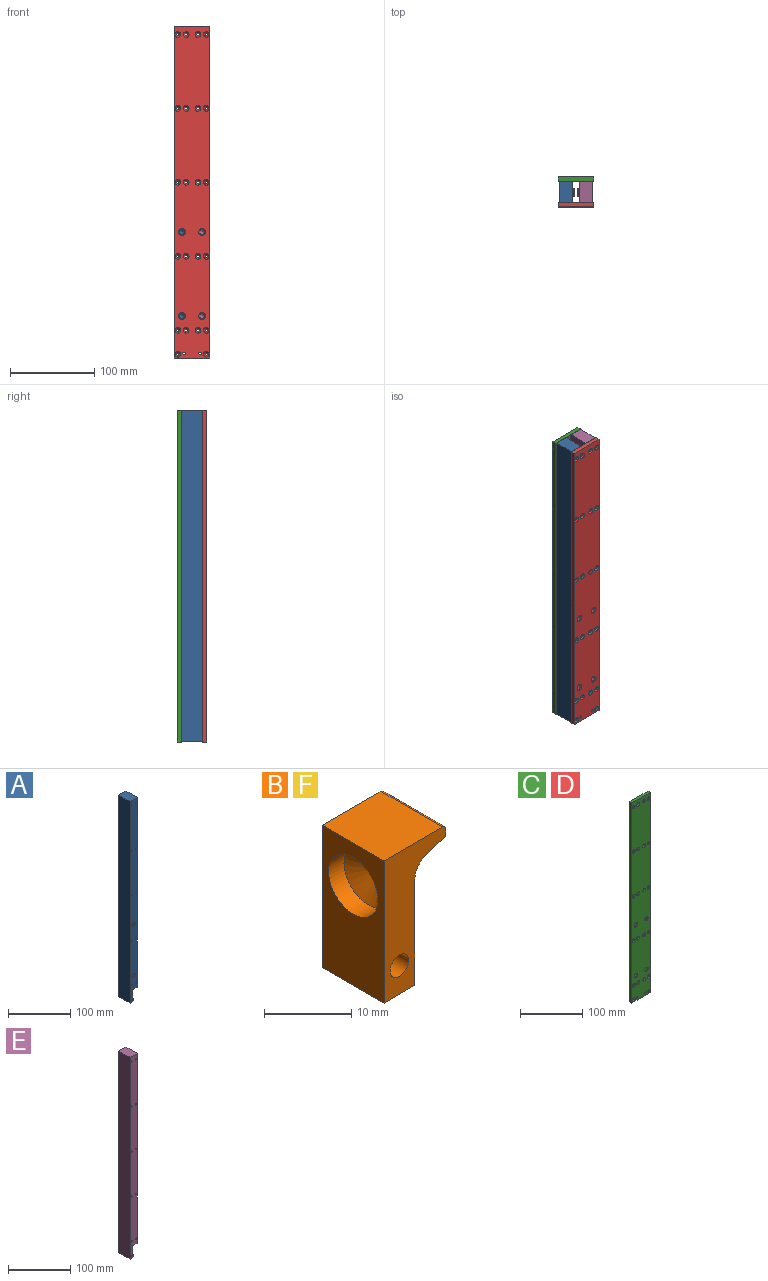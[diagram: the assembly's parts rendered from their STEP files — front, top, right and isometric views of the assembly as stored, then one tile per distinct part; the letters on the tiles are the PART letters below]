
ASSEMBLY  parts=6 mates=5
PART A: 29 faces, bbox 16x25.2x395 mm
  f0: plane 25.2x16mm, normal (0,0,1), area 403.2mm2, adj f1,f3,f4,f5
  f1: plane 395x25.2mm, normal (-1,0,0), area 9954mm2, adj f0,f2,f4,f5
  f2: plane 25.2x8mm, normal (0,0,-1), area 201.6mm2, adj f1,f4,f5,f9
  f3: plane 372x25.2mm, normal (1,0,0), area 9374.4mm2, adj f0,f4,f5,f6
  f4: plane 395x16mm, normal (0,-1,0), area 5921.7mm2, adj f0,f1,f2,f3,f6,f7,f8,f9
  f5: plane 395x16mm, normal (0,1,0), area 6022.2mm2, adj f0,f1,f2,f3,f6,f7,f8,f9
  f6: plane 25.2x10mm, normal (0,0,-1), area 252mm2, adj f3,f4,f5,f7
  f7: plane 25.2x18mm, normal (1,0,0), area 403.3mm2, adj f4,f5,f6,f8,f11
  f8: plane 25.2x2mm, normal (0,0,1), area 50.4mm2, adj f4,f5,f7,f9
  f9: plane 25.2x5mm, normal (1,0,0), area 126mm2, adj f2,f4,f5,f8
  f10: cone r=0mm half-angle=59deg, axis (1,0,0), area 58.6mm2, adj f11
  f11: cylinder r=4mm len=8mm, axis (1,0,0), area 50.3mm2, adj f7,f10
  f12: cylinder r=1.5mm len=25.2mm, axis (0,-1,0), area 237.5mm2, adj f4,f5
  f13: cylinder r=1.5mm len=25.2mm, axis (0,-1,0), area 237.5mm2, adj f4,f5
  f14: cylinder r=1.5mm len=25.2mm, axis (0,-1,0), area 237.5mm2, adj f4,f5
  f15: cylinder r=1.5mm len=25.2mm, axis (0,-1,0), area 237.5mm2, adj f4,f5
  f16: cylinder r=1.5mm len=25.2mm, axis (0,-1,0), area 237.5mm2, adj f4,f5
  f17: cylinder r=1.5mm len=25.2mm, axis (0,-1,0), area 237.5mm2, adj f4,f5
  f18: cylinder r=1.5mm len=25.2mm, axis (0,-1,0), area 237.5mm2, adj f4,f5
  f19: cylinder r=1.5mm len=25.2mm, axis (0,-1,0), area 237.5mm2, adj f4,f5
  f20: cylinder r=1.5mm len=25.2mm, axis (0,-1,0), area 237.5mm2, adj f4,f5
  f21: cylinder r=1.5mm len=25.2mm, axis (0,-1,0), area 237.5mm2, adj f4,f5
  f22: cylinder r=1.5mm len=25.2mm, axis (0,-1,0), area 237.5mm2, adj f4,f5
  f23: cone r=0mm half-angle=59deg, axis (0,-1,0), area 33mm2, adj f24
  f24: cylinder r=3mm len=6mm, axis (0,-1,0), area 75.4mm2, adj f23,f28
  f25: cone r=0mm half-angle=59deg, axis (0,-1,0), area 33mm2, adj f26
  f26: cylinder r=3mm len=6mm, axis (0,-1,0), area 75.4mm2, adj f25,f27
  f27: cone r=3mm half-angle=45deg, axis (0,-1,0), area 31.1mm2, adj f4,f26
  f28: cone r=3mm half-angle=45deg, axis (0,-1,0), area 31.1mm2, adj f4,f24
PART B: 13 faces, bbox 10x10x20 mm
  f0: plane 10x9.5mm, normal (0,0,1), area 95mm2, adj f1,f4,f5,f9
  f1: plane 20x10mm, normal (-1,0,0), area 149.7mm2, adj f0,f2,f4,f5,f12
  f2: plane 10x5mm, normal (0,0,-1), area 50mm2, adj f1,f4,f5,f6
  f3: plane 10x1.08mm, normal (1,0,0), area 10.8mm2, adj f4,f5,f7,f9
  f4: plane 20x10mm, normal (0,-1,0), area 105.3mm2, adj f0,f1,f2,f3,f6,f7,f8,f9
  f5: plane 20x10mm, normal (0,1,0), area 105.3mm2, adj f0,f1,f2,f3,f6,f7,f8,f9
  f6: plane 14.74x10mm, normal (1,0,0), area 147.4mm2, adj f2,f4,f5,f8
  f7: plane 10x2.82mm, normal (0.27,0,-0.96), area 29.3mm2, adj f3,f4,f5,f8
  f8: cylinder r=3mm len=10mm, axis (0,1,0), area 38.8mm2, adj f4,f5,f6,f7
  f9: cylinder r=0.5mm len=10mm, axis (0,1,0), area 7.9mm2, adj f0,f3,f4,f5
  f10: cylinder r=1.5mm len=10mm, axis (0,-1,0), area 94.2mm2, adj f4,f5
  f11: cone r=0mm half-angle=59deg, axis (-1,0,0), area 58.6mm2, adj f12
  f12: cylinder r=4mm len=8mm, axis (-1,0,0), area 62.8mm2, adj f1,f11
PART C: 64 faces, bbox 42x5x395 mm
  f0: plane 42x5mm, normal (0,0,1), area 210mm2, adj f1,f3,f4,f5
  f1: plane 395x5mm, normal (-1,0,0), area 1975mm2, adj f0,f2,f4,f5
  f2: plane 42x5mm, normal (0,0,-1), area 210mm2, adj f1,f3,f4,f5
  f3: plane 395x5mm, normal (1,0,0), area 1975mm2, adj f0,f2,f4,f5
  f4: plane 395x42mm, normal (0,-1,0), area 15594.5mm2, adj f0,f1,f2,f3,f7,f9,f11,f13
  f5: plane 395x42mm, normal (0,1,0), area 16222.4mm2, adj f0,f1,f2,f3,f6,f8,f10,f12
  f6: cylinder r=1.65mm len=3.3mm, axis (0,-1,0), area 34.1mm2, adj f5,f7
  f7: cone r=1.65mm half-angle=45deg, axis (0,-1,0), area 38.1mm2, adj f4,f6
  f8: cylinder r=1.65mm len=3.3mm, axis (0,-1,0), area 34.1mm2, adj f5,f9
  f9: cone r=1.65mm half-angle=45deg, axis (0,-1,0), area 38.1mm2, adj f4,f8
  f10: cylinder r=1.65mm len=3.3mm, axis (0,-1,0), area 34.1mm2, adj f5,f11
  f11: cone r=1.65mm half-angle=45deg, axis (0,-1,0), area 38.1mm2, adj f4,f10
  f12: cylinder r=1.65mm len=3.3mm, axis (0,-1,0), area 34.1mm2, adj f5,f13
  f13: cone r=1.65mm half-angle=45deg, axis (0,-1,0), area 38.1mm2, adj f4,f12
  f14: cylinder r=1.65mm len=3.3mm, axis (0,-1,0), area 34.1mm2, adj f5,f15
  f15: cone r=1.65mm half-angle=45deg, axis (0,-1,0), area 38.1mm2, adj f4,f14
  f16: cylinder r=1.65mm len=3.3mm, axis (0,-1,0), area 34.1mm2, adj f5,f17
  f17: cone r=1.65mm half-angle=45deg, axis (0,-1,0), area 38.1mm2, adj f4,f16
  f18: cylinder r=1.65mm len=3.3mm, axis (0,-1,0), area 34.1mm2, adj f5,f19
  f19: cone r=1.65mm half-angle=45deg, axis (0,-1,0), area 38.1mm2, adj f4,f18
  f20: cylinder r=1.65mm len=3.3mm, axis (0,-1,0), area 34.1mm2, adj f5,f21
  f21: cone r=1.65mm half-angle=45deg, axis (0,-1,0), area 38.1mm2, adj f4,f20
  f22: cylinder r=1.65mm len=3.3mm, axis (0,-1,0), area 34.1mm2, adj f5,f23
  f23: cone r=1.65mm half-angle=45deg, axis (0,-1,0), area 38.1mm2, adj f4,f22
  f24: cylinder r=1.65mm len=3.3mm, axis (0,-1,0), area 34.1mm2, adj f5,f25
  f25: cone r=1.65mm half-angle=45deg, axis (0,-1,0), area 38.1mm2, adj f4,f24
  f26: cylinder r=1.65mm len=3.3mm, axis (0,-1,0), area 34.1mm2, adj f5,f27
  f27: cone r=1.65mm half-angle=45deg, axis (0,-1,0), area 38.1mm2, adj f4,f26
  f28: cylinder r=1.65mm len=3.3mm, axis (0,-1,0), area 34.1mm2, adj f5,f29
  f29: cone r=1.65mm half-angle=45deg, axis (0,-1,0), area 38.1mm2, adj f4,f28
  f30: cylinder r=1.65mm len=3.3mm, axis (0,-1,0), area 34.1mm2, adj f5,f31
  f31: cone r=1.65mm half-angle=45deg, axis (0,-1,0), area 38.1mm2, adj f4,f30
  f32: cylinder r=1.65mm len=3.3mm, axis (0,-1,0), area 34.1mm2, adj f5,f33
  f33: cone r=1.65mm half-angle=45deg, axis (0,-1,0), area 38.1mm2, adj f4,f32
  f34: cylinder r=1.65mm len=3.3mm, axis (0,-1,0), area 34.1mm2, adj f5,f35
  f35: cone r=1.65mm half-angle=45deg, axis (0,-1,0), area 38.1mm2, adj f4,f34
  f36: cylinder r=1.65mm len=3.3mm, axis (0,-1,0), area 34.1mm2, adj f5,f37
  f37: cone r=1.65mm half-angle=45deg, axis (0,-1,0), area 38.1mm2, adj f4,f36
  f38: cylinder r=1.65mm len=3.3mm, axis (0,-1,0), area 34.1mm2, adj f5,f39
  f39: cone r=1.65mm half-angle=45deg, axis (0,-1,0), area 38.1mm2, adj f4,f38
  f40: cylinder r=1.65mm len=3.3mm, axis (0,-1,0), area 34.1mm2, adj f5,f41
  f41: cone r=1.65mm half-angle=45deg, axis (0,-1,0), area 38.1mm2, adj f4,f40
  f42: cylinder r=1.65mm len=3.3mm, axis (0,-1,0), area 34.1mm2, adj f5,f43
  f43: cone r=1.65mm half-angle=45deg, axis (0,-1,0), area 38.1mm2, adj f4,f42
  f44: cylinder r=1.65mm len=3.3mm, axis (0,-1,0), area 34.1mm2, adj f5,f45
  f45: cone r=1.65mm half-angle=45deg, axis (0,-1,0), area 38.1mm2, adj f4,f44
  f46: cylinder r=1.65mm len=3.3mm, axis (0,-1,0), area 34.1mm2, adj f5,f47
  f47: cone r=1.65mm half-angle=45deg, axis (0,-1,0), area 38.1mm2, adj f4,f46
  f48: cylinder r=1.65mm len=3.3mm, axis (0,-1,0), area 34.1mm2, adj f5,f49
  f49: cone r=1.65mm half-angle=45deg, axis (0,-1,0), area 38.1mm2, adj f4,f48
  f50: cylinder r=1.5mm len=3mm, axis (0,1,0), area 18.8mm2, adj f4,f51
  f51: plane 6.5x6.5mm, normal (0,1,0), area 26.1mm2, adj f50,f52
  f52: cylinder r=3.25mm len=6.5mm, axis (0,1,0), area 61.3mm2, adj f5,f51
  f53: cylinder r=1.5mm len=3mm, axis (0,1,0), area 18.8mm2, adj f4,f54
  f54: plane 6.5x6.5mm, normal (0,1,0), area 26.1mm2, adj f53,f55
  f55: cylinder r=3.25mm len=6.5mm, axis (0,1,0), area 61.3mm2, adj f5,f54
  f56: cylinder r=3mm len=6mm, axis (0,-1,0), area 75.4mm2, adj f5,f62
  f57: cylinder r=3mm len=6mm, axis (0,-1,0), area 75.4mm2, adj f5,f63
  f58: cylinder r=3mm len=6mm, axis (0,-1,0), area 75.4mm2, adj f5,f61
  f59: cylinder r=3mm len=6mm, axis (0,-1,0), area 75.4mm2, adj f5,f60
  f60: cone r=3mm half-angle=45deg, axis (0,-1,0), area 31.1mm2, adj f4,f59
  f61: cone r=3mm half-angle=45deg, axis (0,-1,0), area 31.1mm2, adj f4,f58
  f62: cone r=3mm half-angle=45deg, axis (0,-1,0), area 31.1mm2, adj f4,f56
  f63: cone r=3mm half-angle=45deg, axis (0,-1,0), area 31.1mm2, adj f4,f57
PART D: same geometry as C
PART E: 29 faces, bbox 16x25.2x395 mm
  f0: plane 25.2x16mm, normal (0,0,1), area 403.2mm2, adj f1,f3,f4,f5
  f1: plane 395x25.2mm, normal (-1,0,0), area 9954mm2, adj f0,f2,f4,f5
  f2: plane 25.2x8mm, normal (0,0,-1), area 201.6mm2, adj f1,f4,f5,f9
  f3: plane 372x25.2mm, normal (1,0,0), area 9374.4mm2, adj f0,f4,f5,f6
  f4: plane 395x16mm, normal (0,-1,0), area 6022.2mm2, adj f0,f1,f2,f3,f6,f7,f8,f9
  f5: plane 395x16mm, normal (0,1,0), area 5921.7mm2, adj f0,f1,f2,f3,f6,f7,f8,f9
  f6: plane 25.2x10mm, normal (0,0,-1), area 252mm2, adj f3,f4,f5,f7
  f7: plane 25.2x18mm, normal (1,0,0), area 403.3mm2, adj f4,f5,f6,f8,f11
  f8: plane 25.2x2mm, normal (0,0,1), area 50.4mm2, adj f4,f5,f7,f9
  f9: plane 25.2x5mm, normal (1,0,0), area 126mm2, adj f2,f4,f5,f8
  f10: cone r=0mm half-angle=59deg, axis (1,0,0), area 58.6mm2, adj f11
  f11: cylinder r=4mm len=8mm, axis (1,0,0), area 50.3mm2, adj f7,f10
  f12: cylinder r=1.5mm len=25.2mm, axis (0,-1,0), area 237.5mm2, adj f4,f5
  f13: cylinder r=1.5mm len=25.2mm, axis (0,-1,0), area 237.5mm2, adj f4,f5
  f14: cylinder r=1.5mm len=25.2mm, axis (0,-1,0), area 237.5mm2, adj f4,f5
  f15: cylinder r=1.5mm len=25.2mm, axis (0,-1,0), area 237.5mm2, adj f4,f5
  f16: cylinder r=1.5mm len=25.2mm, axis (0,-1,0), area 237.5mm2, adj f4,f5
  f17: cylinder r=1.5mm len=25.2mm, axis (0,-1,0), area 237.5mm2, adj f4,f5
  f18: cylinder r=1.5mm len=25.2mm, axis (0,-1,0), area 237.5mm2, adj f4,f5
  f19: cylinder r=1.5mm len=25.2mm, axis (0,-1,0), area 237.5mm2, adj f4,f5
  f20: cylinder r=1.5mm len=25.2mm, axis (0,-1,0), area 237.5mm2, adj f4,f5
  f21: cylinder r=1.5mm len=25.2mm, axis (0,-1,0), area 237.5mm2, adj f4,f5
  f22: cylinder r=1.5mm len=25.2mm, axis (0,-1,0), area 237.5mm2, adj f4,f5
  f23: cone r=0mm half-angle=59deg, axis (0,1,0), area 33mm2, adj f24
  f24: cylinder r=3mm len=6mm, axis (0,1,0), area 75.4mm2, adj f23,f28
  f25: cone r=0mm half-angle=59deg, axis (0,1,0), area 33mm2, adj f26
  f26: cylinder r=3mm len=6mm, axis (0,1,0), area 75.4mm2, adj f25,f27
  f27: cone r=3mm half-angle=45deg, axis (0,1,0), area 31.1mm2, adj f5,f26
  f28: cone r=3mm half-angle=45deg, axis (0,1,0), area 31.1mm2, adj f5,f24
PART F: same geometry as B
PLACE A t=(-202.45,28.91,28.25)mm
PLACE B t=(-204.53,21.31,33.53)mm
PLACE C rot(axis=(0,0,1),180deg) t=(-194.86,28.91,45.29)mm
PLACE D t=(-197.1,3.71,45.29)mm
PLACE E rot(axis=(0,0,1),180deg) t=(-189.52,3.71,28.25)mm
PLACE F rot(axis=(0,0,1),180deg) t=(-187.43,11.31,33.53)mm
MATE parallel F.f1 <-> E.f9  axis (1,0,0) through (-183.88,16.31,11.7)mm
MATE parallel E.f3 <-> A.f3  axis (-1,0,0) through (-191.88,16.31,219.2)mm
MATE parallel C.f30 <-> A.f12  axis (0,-1,0) through (-213.08,28.91,395.2)mm
MATE parallel D.f30 <-> E.f12  axis (0,1,0) through (-178.88,3.71,395.2)mm
MATE parallel B.f1 <-> A.f9  axis (-1,0,0) through (-208.08,16.31,11.7)mm
